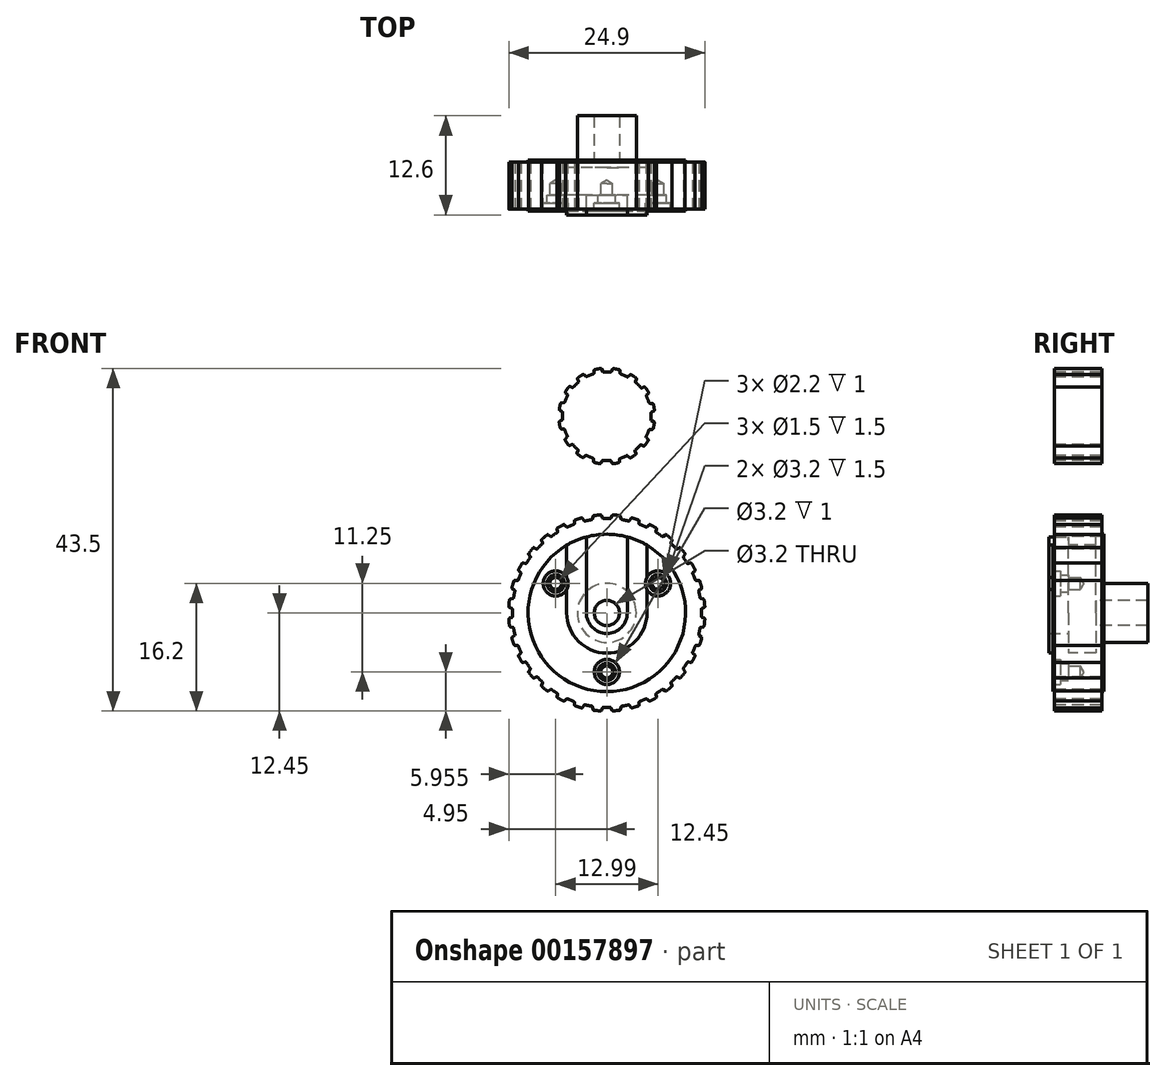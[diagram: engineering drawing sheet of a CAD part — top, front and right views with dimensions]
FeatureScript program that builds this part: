
annotation { "Feature Type Name" : "Feature", "Feature Type Description" : "" }
export const myFeature = defineFeature(function(context is Context, id is Id, definition is map)
    precondition{}
    {
        {
            var Q0;
            Q0=qCreatedBy(makeId("Front.planeOp"),FACE);
            var sketch = newSketch(context, id + "F0", { "sketchPlane" : qUnion([Q0])});
            skArc(sketch, "E0", {"start": v(-2.6, 9.66) * mm, "mid": v(0, -10) * mm, "end": v(2.6, 9.66) * mm});
            skArc(sketch, "E1", {"start": v(-2.6, 0) * mm, "mid": v(0, -2.6) * mm, "end": v(2.6, 0) * mm});
            skLineSegment(sketch, "E2", {"start": v(-2.6, 0) * mm, "end": v(-2.6, 9.66) * mm});
            skLineSegment(sketch, "E3", {"start": v(2.6, 0) * mm, "end": v(2.6, 9.66) * mm});
            skSolve(sketch);
        }
        {
            var Q0;
            Q0 = qSketchRegion(id + "F0", true);
            extrude(context, id + "F1", {"entities" : qUnion([Q0]), "depth" : 2 * mm});
        }
        {
            var Q0;
            Q0=makeQuery(id+"F1.opExtrude","CAP_FACE",FACE,{"disambiguationData":[OSD([sQuery(id+"F0.wireOp",EDGE,"E0"),sQuery(id+"F0.wireOp",EDGE,"E1"),sQuery(id+"F0.wireOp",EDGE,"E2"),sQuery(id+"F0.wireOp",EDGE,"E3")])],"isStart":false});
            var sketch = newSketch(context, id + "F2", { "sketchPlane" : qUnion([Q0])});
            skArc(sketch, "E4.0", {"start": v(-2.6, 0) * mm, "mid": v(0, -2.6) * mm, "end": v(2.6, 0) * mm});
            skLineSegment(sketch, "E5.0", {"start": v(2.6, 0) * mm, "end": v(2.6, 9.66) * mm});
            skLineSegment(sketch, "E6.0", {"start": v(-2.6, 0) * mm, "end": v(-2.6, 9.66) * mm});
            skLineSegment(sketch, "E7.0", {"start": v(-5.1, 0) * mm, "end": v(-5.1, 8.6) * mm});
            skArc(sketch, "E7.1", {"start": v(-5.1, 0) * mm, "mid": v(0, -5.1) * mm, "end": v(5.1, 0) * mm});
            skLineSegment(sketch, "E7.2", {"start": v(5.1, 0) * mm, "end": v(5.1, 8.6) * mm});
            skArc(sketch, "E8", {"start": v(5.1, 8.6) * mm, "mid": v(3.89, 9.21) * mm, "end": v(2.6, 9.66) * mm});
            skArc(sketch, "E9.trimOffspring", {"start": v(-2.6, 9.66) * mm, "mid": v(-3.89, 9.21) * mm, "end": v(-5.1, 8.6) * mm});
            skSolve(sketch);
        }
        {
            var Q0;
            Q0 = qSketchRegion(id + "F2", true);
            extrude(context, id + "F3", {"entities" : qUnion([Q0]), "operationType" : NewBodyOperationType.ADD, "depth" : 0.5 * mm});
        }
        {
            var Q0;
            Q0=makeQuery(id+"F1.opExtrude","CAP_FACE",FACE,{"disambiguationData":[OSD([sQuery(id+"F0.wireOp",EDGE,"E0"),sQuery(id+"F0.wireOp",EDGE,"E1"),sQuery(id+"F0.wireOp",EDGE,"E2"),sQuery(id+"F0.wireOp",EDGE,"E3")])],"isStart":true});
            var sketch = newSketch(context, id + "F4", { "sketchPlane" : qUnion([Q0])});
            skLineSegment(sketch, "E10.0", {"start": v(-5.1, 0) * mm, "end": v(-5.1, 8.6) * mm});
            skArc(sketch, "E11.0", {"start": v(5.1, 0) * mm, "mid": v(0, -5.1) * mm, "end": v(-5.1, 0) * mm});
            skLineSegment(sketch, "E12.0", {"start": v(5.1, 0) * mm, "end": v(5.1, 8.6) * mm});
            skPoint(sketch, "E13.orphan", {"position": v(-2.6, 9.66) * mm});
            skPoint(sketch, "E14.orphan", {"position": v(2.6, 9.66) * mm});
            skArc(sketch, "E15", {"start": v(-5.1, 8.6) * mm, "mid": v(0, -10) * mm, "end": v(5.1, 8.6) * mm});
            skSolve(sketch);
        }
        {
            var Q0;
            {var subQ0=sQuery(id+"F4.wireOp",EDGE,"E10.0");Q0=makeQuery(id+"F4.imprint","IMPRINT",FACE,{"disambiguationData":[TD([[makeQuery(id+"F4.imprint","IMPRINT",EDGE,{"derivedFrom":subQ0}),1.0]])]});}
            extrude(context, id + "F5", {"entities" : qUnion([Q0]), "depth" : 3.5 * mm});
        }
        {
            var Q0;
            Q0=makeQuery(id+"F5.opExtrude","CAP_FACE",FACE,{"disambiguationData":[OSD([sQuery(id+"F4.wireOp",EDGE,"44c54655-4551-4a46-a045-2cd2228b2ac6.0"),sQuery(id+"F4.wireOp",EDGE,"E10.0"),sQuery(id+"F4.wireOp",EDGE,"E11.0"),sQuery(id+"F4.wireOp",EDGE,"E12.0")])],"isStart":false});
            var sketch = newSketch(context, id + "F6", { "sketchPlane" : qUnion([Q0])});
            skCircle(sketch, "E16", {"center": v(0, 0) * mm, "radius": 10 * mm});
            skSolve(sketch);
        }
        {
            var Q0;
            Q0 = qSketchRegion(id + "F6", true);
            extrude(context, id + "F7", {"entities" : qUnion([Q0]), "operationType" : NewBodyOperationType.ADD, "depth" : 1 * mm});
        }
        {
            var Q0;
            Q0=makeQuery(id+"F7.opExtrude","CAP_FACE",FACE,{"disambiguationData":[OSD([sQuery(id+"F6.wireOp",EDGE,"E16")])],"isStart":false});
            var sketch = newSketch(context, id + "F8", { "sketchPlane" : qUnion([Q0])});
            skCircle(sketch, "E17", {"center": v(0, 0) * mm, "radius": 3.75 * mm});
            skSolve(sketch);
        }
        {
            var Q0;
            Q0 = qSketchRegion(id + "F8", true);
            extrude(context, id + "F9", {"entities" : qUnion([Q0]), "operationType" : NewBodyOperationType.ADD, "depth" : 5.6 * mm});
        }
        {
            var Q0;
            Q0=makeQuery(id+"F9.opExtrude","CAP_FACE",FACE,{"disambiguationData":[OSD([sQuery(id+"F8.wireOp",EDGE,"E17")])],"isStart":false});
            var sketch = newSketch(context, id + "F10", { "sketchPlane" : qUnion([Q0])});
            skArc(sketch, "E18", {"start": v(-2.8, 2.5) * mm, "mid": v(0, -3.75) * mm, "end": v(2.8, 2.5) * mm});
            skSolve(sketch);
        }
        {
            var Q0;
            Q0=sQuery(id+"F10.wireOp",VERTEX,"E18.center");
            var Q1;
            Q1=makeQuery(id+"F5.opExtrude","SWEPT_BODY",BODY,{"disambiguationData":[OSD([sQuery(id+"F4.wireOp",EDGE,"44c54655-4551-4a46-a045-2cd2228b2ac6.0"),sQuery(id+"F4.wireOp",EDGE,"E10.0"),sQuery(id+"F4.wireOp",EDGE,"E11.0"),sQuery(id+"F4.wireOp",EDGE,"E12.0")])]});
            hole(context, id + "F11", {"style" : HoleStyle.SIMPLE, "endStyle" : HoleEndStyle.THROUGH, "standardTappedOrClearance" : lookupTablePath({ "standard" : "ISO", "engagement" : "75%", "pitch" : "0.75 mm", "size" : "M4", "type" : "Tapped" }), "standardBlindInLast" : lookupTablePath({ "standard" : "ISO", "engagement" : "75%", "pitch" : "0.75 mm", "size" : "M4", "type" : "Tapped" }), "holeDiameter" : 3.2 * mm, "locations" : qUnion([Q0]), "scope" : qUnion([Q1]), "isTappedThrough" : true, "showTappedDepth" : true, "startStyle" : HoleStartStyle.SKETCH});
        }
        {
            var Q0;
            Q0=makeQuery(id+"F1.opExtrude","CAP_FACE",FACE,{"disambiguationData":[OSD([sQuery(id+"F0.wireOp",EDGE,"E0"),sQuery(id+"F0.wireOp",EDGE,"E1"),sQuery(id+"F0.wireOp",EDGE,"E2"),sQuery(id+"F0.wireOp",EDGE,"E3")])],"isStart":false});
            var sketch = newSketch(context, id + "F12", { "sketchPlane" : qUnion([Q0])});
            skArc(sketch, "E19", {"start": v(-0.38, -7.5) * mm, "mid": v(0, -7.5) * mm, "end": v(0.38, -7.5) * mm});
            skCircle(sketch, "E20", {"center": v(0, -7.5) * mm, "radius": 0.38 * mm});
            skLineSegment(sketch, "E21", {"start": v(6.32, 3.65) * mm, "end": v(6.67, 3.85) * mm});
            skCircle(sketch, "E22", {"center": v(6.5, 3.75) * mm, "radius": 0.2 * mm});
            skArc(sketch, "E23.trimOffspring", {"start": v(6.6, 3.57) * mm, "mid": v(6.5, 3.75) * mm, "end": v(6.39, 3.93) * mm});
            skCircle(sketch, "E24.MirrorC", {"center": v(-6.5, 3.75) * mm, "radius": 0.2 * mm});
            skSolve(sketch);
        }
        {
            var Q0;
            Q0=sQuery(id+"F12.wireOp",VERTEX,"E24.MirrorC.center");
            var Q1;
            Q1=sQuery(id+"F12.wireOp",VERTEX,"E22.center");
            var Q2;
            Q2=sQuery(id+"F12.wireOp",VERTEX,"E20.center");
            var Q3;
            Q3=makeQuery(id+"F1.opExtrude","SWEPT_BODY",BODY,{"disambiguationData":[OSD([sQuery(id+"F0.wireOp",EDGE,"E0"),sQuery(id+"F0.wireOp",EDGE,"E1"),sQuery(id+"F0.wireOp",EDGE,"E2"),sQuery(id+"F0.wireOp",EDGE,"E3")])]});
            hole(context, id + "F13", {"style" : HoleStyle.C_BORE, "endStyle" : HoleEndStyle.THROUGH, "holeDiameter" : 2.2 * mm, "cBoreDiameter" : 3.2 * mm, "cBoreDepth" : 1 * mm, "locations" : qUnion([Q0, Q1, Q2]), "scope" : qUnion([Q3]), "isTappedThrough" : true, "startStyle" : HoleStartStyle.SKETCH});
        }
        {
            var Q0;
            Q0=sQuery(id+"F12.wireOp",VERTEX,"E24.MirrorC.center");
            var Q1;
            Q1=sQuery(id+"F12.wireOp",VERTEX,"E20.center");
            var Q2;
            Q2=sQuery(id+"F12.wireOp",VERTEX,"E22.center");
            var Q3;
            Q3=makeQuery(id+"F5.opExtrude","SWEPT_BODY",BODY,{"disambiguationData":[OSD([sQuery(id+"F4.wireOp",EDGE,"44c54655-4551-4a46-a045-2cd2228b2ac6.0"),sQuery(id+"F4.wireOp",EDGE,"E10.0"),sQuery(id+"F4.wireOp",EDGE,"E11.0"),sQuery(id+"F4.wireOp",EDGE,"E12.0")])]});
            hole(context, id + "F14", {"style" : HoleStyle.SIMPLE, "endStyle" : HoleEndStyle.BLIND, "holeDiameter" : 1.5 * mm, "holeDepth" : 3.5 * mm, "locations" : qUnion([Q0, Q1, Q2]), "scope" : qUnion([Q3]), "startStyle" : HoleStartStyle.SKETCH});
        }
        {
            var Q0;
            Q0=qCreatedBy(makeId("Front.planeOp"),FACE);
            cPlane(context, id + "F15", {"entities" : qUnion([Q0]), "cplaneType" : CPlaneType.OFFSET, "offset" : 4.25 * mm, "oppositeDirection" : true, "width" : 150 * mm, "height" : 150 * mm});
        }
        {
            var Q0;
            Q0=qCreatedBy(id+"F15.planeOp",FACE);
            var sketch = newSketch(context, id + "F16", { "sketchPlane" : qUnion([Q0])});
            skCircle(sketch, "E25", {"center": v(0, 0) * mm, "radius": 10 * mm});
            skCircle(sketch, "E26", {"center": v(0, 0) * mm, "radius": 12.47 * mm});
            skSolve(sketch);
        }
        {
            var Q0;
            Q0 = qSketchRegion(id + "F16", true);
            extrude(context, id + "F17", {"entities" : qUnion([Q0]), "operationType" : NewBodyOperationType.ADD, "depth" : 6 * mm});
        }
        {
            var Q0;
            Q0=qCreatedBy(makeId("Front.planeOp"),FACE);
            cPlane(context, id + "F18", {"entities" : qUnion([Q0]), "cplaneType" : CPlaneType.OFFSET, "offset" : 1.25 * mm, "oppositeDirection" : true, "width" : 150 * mm, "height" : 150 * mm});
        }
        {
            var Q0;
            Q0=qCreatedBy(id+"F18.planeOp",FACE);
            var sketch = newSketch(context, id + "F19", { "sketchPlane" : qUnion([Q0])});
            skArc(sketch, "E27", {"start": v(0.42, 12) * mm, "mid": v(0, 12) * mm, "end": v(-0.42, 12) * mm});
            skLineSegment(sketch, "E28", {"start": v(0.67, 12.37) * mm, "end": v(0.55, 12.07) * mm});
            skLineSegment(sketch, "E29", {"start": v(-0.55, 12.07) * mm, "end": v(-0.67, 12.37) * mm});
            skPoint(sketch, "E30.visualSharp", {"position": v(-0.51, 11.99) * mm});
            skArc(sketch, "E30.filletArc", {"start": v(-0.55, 12.07) * mm, "mid": v(-0.5, 12.01) * mm, "end": v(-0.42, 12) * mm});
            skPoint(sketch, "E31.visualSharp", {"position": v(0.51, 11.99) * mm});
            skArc(sketch, "E31.filletArc", {"start": v(0.42, 12) * mm, "mid": v(0.5, 12.01) * mm, "end": v(0.55, 12.07) * mm});
            skPoint(sketch, "E32.visualSharp", {"position": v(-0.7, 12.46) * mm});
            skArc(sketch, "E32.filletArc", {"start": v(-0.67, 12.37) * mm, "mid": v(-0.72, 12.43) * mm, "end": v(-0.8, 12.45) * mm});
            skPoint(sketch, "E33.visualSharp", {"position": v(0.7, 12.46) * mm});
            skArc(sketch, "E33.filletArc", {"start": v(0.8, 12.45) * mm, "mid": v(0.72, 12.43) * mm, "end": v(0.67, 12.37) * mm});
            skArc(sketch, "E34.filletArc", {"start": v(-0.15, 1.02) * mm, "mid": v(-0.02, 0.91) * mm, "end": v(0.1, 1.03) * mm});
            skLineSegment(sketch, "E35", {"start": v(-0.8, 12.45) * mm, "end": v(-0.8, 12.84) * mm});
            skLineSegment(sketch, "E36", {"start": v(-0.8, 12.84) * mm, "end": v(0.8, 12.84) * mm});
            skLineSegment(sketch, "E37", {"start": v(0.8, 12.84) * mm, "end": v(0.8, 12.45) * mm});
            skSolve(sketch);
        }
        {
            var Q0;
            Q0 = qSketchRegion(id + "F19", true);
            extrude(context, id + "F20", {"entities" : qUnion([Q0]), "operationType" : NewBodyOperationType.REMOVE, "oppositeDirection" : true, "depth" : 6.5 * mm, "symmetric" : true});
        }
        {
            var Q0;
            Q0=qCreatedBy(makeId("Right.planeOp"),FACE);
            var sketch = newSketch(context, id + "F21", { "sketchPlane" : qUnion([Q0])});
            skLineSegment(sketch, "E38", {"start": v(-10.84, 0) * mm, "end": v(21.43, 0) * mm});
            skSolve(sketch);
        }
        {
            var Q0;
            Q0=makeQuery(id+"F20.boolean.opBoolean","COPY",FACE,{"derivedFrom":makeQuery(id+"F20.opExtrude","SWEPT_FACE",FACE,{"disambiguationData":[OSD([sQuery(id+"F19.wireOp",EDGE,"E32.filletArc")])]})});
            var Q1;
            Q1=makeQuery(id+"F20.boolean.opBoolean","COPY",FACE,{"derivedFrom":makeQuery(id+"F20.opExtrude","SWEPT_FACE",FACE,{"disambiguationData":[OSD([sQuery(id+"F19.wireOp",EDGE,"E29")])]})});
            var Q2;
            Q2=makeQuery(id+"F20.boolean.opBoolean","COPY",FACE,{"derivedFrom":makeQuery(id+"F20.opExtrude","SWEPT_FACE",FACE,{"disambiguationData":[OSD([sQuery(id+"F19.wireOp",EDGE,"E30.filletArc")])]})});
            var Q3;
            Q3=makeQuery(id+"F20.boolean.opBoolean","COPY",FACE,{"derivedFrom":makeQuery(id+"F20.opExtrude","SWEPT_FACE",FACE,{"disambiguationData":[OSD([sQuery(id+"F19.wireOp",EDGE,"E27")])]})});
            var Q4;
            Q4=makeQuery(id+"F20.boolean.opBoolean","COPY",FACE,{"derivedFrom":makeQuery(id+"F20.opExtrude","SWEPT_FACE",FACE,{"disambiguationData":[OSD([sQuery(id+"F19.wireOp",EDGE,"E31.filletArc")])]})});
            var Q5;
            Q5=makeQuery(id+"F20.boolean.opBoolean","COPY",FACE,{"derivedFrom":makeQuery(id+"F20.opExtrude","SWEPT_FACE",FACE,{"disambiguationData":[OSD([sQuery(id+"F19.wireOp",EDGE,"E28")])]})});
            var Q6;
            Q6=makeQuery(id+"F20.boolean.opBoolean","COPY",FACE,{"derivedFrom":makeQuery(id+"F20.opExtrude","SWEPT_FACE",FACE,{"disambiguationData":[OSD([sQuery(id+"F19.wireOp",EDGE,"E33.filletArc")])]})});
            var Q7;
            Q7=sQuery(id+"F21.wireOp",EDGE,"E38");
            circularPattern(context, id + "F22", {"patternType" : PatternType.FACE, "operationType" : NewBodyOperationType.REMOVE, "faces" : qUnion([Q0, Q1, Q2, Q3, Q4, Q5, Q6]), "axis" : qUnion([Q7]), "angle" : 11.25 * degree, "instanceCount" : 32});
        }
        {
            var Q0;
            Q0=qCreatedBy(id+"F15.planeOp",FACE);
            var sketch = newSketch(context, id + "F23", { "sketchPlane" : qUnion([Q0])});
            skCircle(sketch, "E39", {"center": v(0, 25) * mm, "radius": 6.1 * mm});
            skSolve(sketch);
        }
        {
            var Q0;
            Q0 = qSketchRegion(id + "F23", true);
            extrude(context, id + "F24", {"entities" : qUnion([Q0]), "depth" : 6 * mm});
        }
        {
            var Q0;
            Q0=qCreatedBy(id+"F18.planeOp",FACE);
            var sketch = newSketch(context, id + "F25", { "sketchPlane" : qUnion([Q0])});
            skArc(sketch, "E40", {"start": v(0.46, 30.6) * mm, "mid": v(0.04, 30.62) * mm, "end": v(-0.39, 30.61) * mm});
            skLineSegment(sketch, "E41", {"start": v(0.72, 30.97) * mm, "end": v(0.59, 30.68) * mm});
            skLineSegment(sketch, "E42", {"start": v(-0.51, 30.69) * mm, "end": v(-0.65, 30.98) * mm});
            skPoint(sketch, "E43.orphan", {"position": v(0.6, 31.64) * mm});
            skPoint(sketch, "E44.orphan", {"position": v(-0.6, 31.64) * mm});
            skPoint(sketch, "E45.visualSharp", {"position": v(0.55, 30.6) * mm});
            skArc(sketch, "E45.filletArc", {"start": v(0.46, 30.6) * mm, "mid": v(0.54, 30.62) * mm, "end": v(0.59, 30.68) * mm});
            skPoint(sketch, "E46.visualSharp", {"position": v(-0.48, 30.6) * mm});
            skArc(sketch, "E46.filletArc", {"start": v(-0.51, 30.69) * mm, "mid": v(-0.46, 30.63) * mm, "end": v(-0.39, 30.61) * mm});
            skPoint(sketch, "E47.visualSharp", {"position": v(0.76, 31.05) * mm});
            skArc(sketch, "E47.filletArc", {"start": v(0.86, 31.04) * mm, "mid": v(0.78, 31.02) * mm, "end": v(0.72, 30.97) * mm});
            skPoint(sketch, "E48.visualSharp", {"position": v(-0.7, 31.06) * mm});
            skArc(sketch, "E48.filletArc", {"start": v(-0.65, 30.98) * mm, "mid": v(-0.7, 31.03) * mm, "end": v(-0.78, 31.05) * mm});
            skLineSegment(sketch, "E49", {"start": v(-0.78, 31.05) * mm, "end": v(-0.78, 31.53) * mm});
            skLineSegment(sketch, "E50", {"start": v(-0.78, 31.53) * mm, "end": v(0.86, 31.53) * mm});
            skLineSegment(sketch, "E51", {"start": v(0.86, 31.04) * mm, "end": v(0.86, 31.53) * mm});
            skSolve(sketch);
        }
        {
            var Q0;
            Q0=qCreatedBy(makeId("Right.planeOp"),FACE);
            var sketch = newSketch(context, id + "F26", { "sketchPlane" : qUnion([Q0])});
            skLineSegment(sketch, "E52", {"start": v(-8.2, 25) * mm, "end": v(13.86, 25) * mm});
            skSolve(sketch);
        }
        {
            var Q0;
            Q0 = qSketchRegion(id + "F25", true);
            extrude(context, id + "F27", {"entities" : qUnion([Q0]), "operationType" : NewBodyOperationType.REMOVE, "oppositeDirection" : true, "depth" : 6 * mm, "symmetric" : true});
        }
        {
            var Q0;
            Q0=makeQuery(id+"F27.boolean.opBoolean","COPY",FACE,{"derivedFrom":makeQuery(id+"F27.opExtrude","SWEPT_FACE",FACE,{"disambiguationData":[OSD([sQuery(id+"F25.wireOp",EDGE,"E48.filletArc")])]})});
            var Q1;
            Q1=makeQuery(id+"F27.boolean.opBoolean","COPY",FACE,{"derivedFrom":makeQuery(id+"F27.opExtrude","SWEPT_FACE",FACE,{"disambiguationData":[OSD([sQuery(id+"F25.wireOp",EDGE,"E42")])]})});
            var Q2;
            Q2=makeQuery(id+"F27.boolean.opBoolean","COPY",FACE,{"derivedFrom":makeQuery(id+"F27.opExtrude","SWEPT_FACE",FACE,{"disambiguationData":[OSD([sQuery(id+"F25.wireOp",EDGE,"E46.filletArc")])]})});
            var Q3;
            Q3=makeQuery(id+"F27.boolean.opBoolean","COPY",FACE,{"derivedFrom":makeQuery(id+"F27.opExtrude","SWEPT_FACE",FACE,{"disambiguationData":[OSD([sQuery(id+"F25.wireOp",EDGE,"E40")])]})});
            var Q4;
            Q4=makeQuery(id+"F27.boolean.opBoolean","COPY",FACE,{"derivedFrom":makeQuery(id+"F27.opExtrude","SWEPT_FACE",FACE,{"disambiguationData":[OSD([sQuery(id+"F25.wireOp",EDGE,"E45.filletArc")])]})});
            var Q5;
            Q5=makeQuery(id+"F27.boolean.opBoolean","COPY",FACE,{"derivedFrom":makeQuery(id+"F27.opExtrude","SWEPT_FACE",FACE,{"disambiguationData":[OSD([sQuery(id+"F25.wireOp",EDGE,"E41")])]})});
            var Q6;
            Q6=makeQuery(id+"F27.boolean.opBoolean","COPY",FACE,{"derivedFrom":makeQuery(id+"F27.opExtrude","SWEPT_FACE",FACE,{"disambiguationData":[OSD([sQuery(id+"F25.wireOp",EDGE,"E47.filletArc")])]})});
            var Q7;
            Q7=sQuery(id+"F26.wireOp",EDGE,"E52");
            circularPattern(context, id + "F28", {"patternType" : PatternType.FACE, "operationType" : NewBodyOperationType.REMOVE, "faces" : qUnion([Q0, Q1, Q2, Q3, Q4, Q5, Q6]), "axis" : qUnion([Q7]), "angle" : 22.5 * degree, "instanceCount" : 16});
        }
    });
